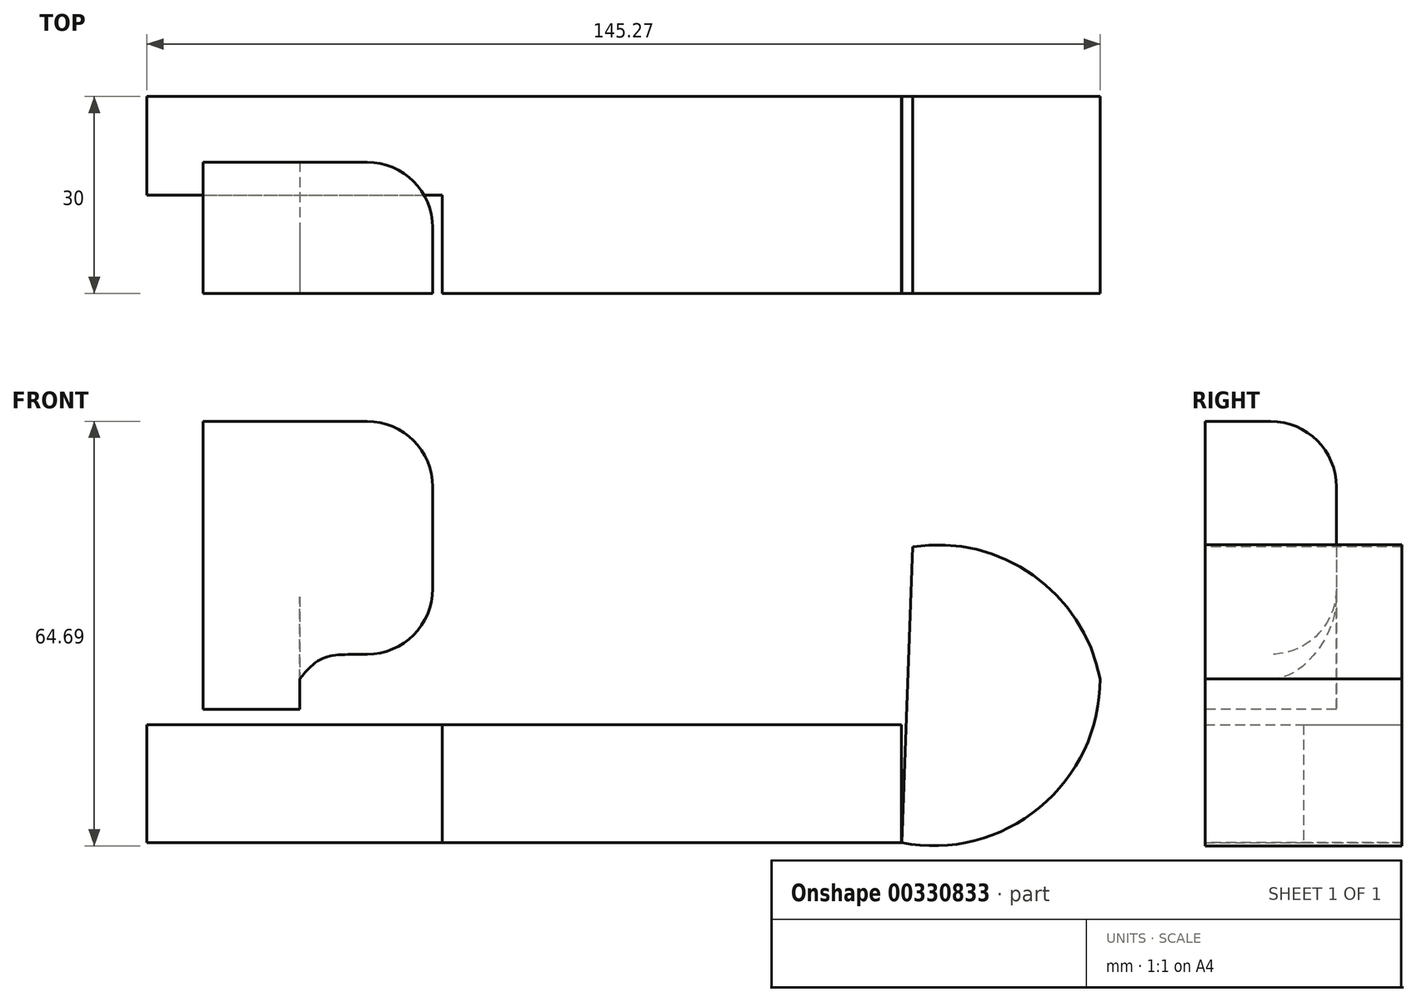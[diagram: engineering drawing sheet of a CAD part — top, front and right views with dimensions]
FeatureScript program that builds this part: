
annotation { "Feature Type Name" : "Feature", "Feature Type Description" : "" }
export const myFeature = defineFeature(function(context is Context, id is Id, definition is map)
    precondition{}
    {
        {
            var Q0;
            Q0=qCreatedBy(makeId("Top.planeOp"),FACE);
            var sketch = newSketch(context, id + "F0", { "sketchPlane" : qUnion([Q0])});
            skLineSegment(sketch, "E0.bottom", {"start": v(45.03, 0) * mm, "end": v(115, 0) * mm});
            skLineSegment(sketch, "E0.top", {"start": v(0, 30) * mm, "end": v(115, 30) * mm});
            skLineSegment(sketch, "E0.left", {"start": v(0, 15) * mm, "end": v(0, 30) * mm});
            skLineSegment(sketch, "E0.right", {"start": v(115, 0) * mm, "end": v(115, 30) * mm});
            skLineSegment(sketch, "E1", {"start": v(0, 30) * mm, "end": v(0, 15) * mm});
            skLineSegment(sketch, "E2", {"start": v(0, 15) * mm, "end": v(45.03, 15) * mm});
            skLineSegment(sketch, "E3", {"start": v(45.03, 0) * mm, "end": v(45.03, 15) * mm});
            skPoint(sketch, "E4.orphan", {"position": v(0, 0) * mm});
            skSolve(sketch);
        }
        {
            var Q0;
            Q0 = qSketchRegion(id + "F0", true);
            extrude(context, id + "F1", {"entities" : qUnion([Q0]), "depth" : 18 * mm});
        }
        {
            var Q0;
            Q0=qCreatedBy(makeId("Front.planeOp"),FACE);
            var sketch = newSketch(context, id + "F2", { "sketchPlane" : qUnion([Q0])});
            skLineSegment(sketch, "E5", {"start": v(115.04, 0) * mm, "end": v(124.63, 0) * mm});
            skArc(sketch, "E6", {"start": v(115.04, 0) * mm, "mid": v(136.04, 5.37) * mm, "end": v(145.27, 24.98) * mm});
            skArc(sketch, "E7", {"start": v(145.27, 24.98) * mm, "mid": v(135.05, 40.8) * mm, "end": v(116.72, 45.14) * mm});
            skLineSegment(sketch, "E8", {"start": v(116.72, 45.14) * mm, "end": v(115.04, 0) * mm});
            skSolve(sketch);
        }
        {
            var Q0;
            Q0 = qSketchRegion(id + "F2", true);
            extrude(context, id + "F3", {"entities" : qUnion([Q0]), "oppositeDirection" : true, "depth" : 30 * mm});
        }
        {
            var Q0;
            Q0=qCreatedBy(makeId("Front.planeOp"),FACE);
            var sketch = newSketch(context, id + "F4", { "sketchPlane" : qUnion([Q0])});
            skLineSegment(sketch, "E9", {"start": v(8.54, 64.23) * mm, "end": v(43.55, 64.23) * mm});
            skLineSegment(sketch, "E10", {"start": v(43.55, 64.23) * mm, "end": v(43.55, 34.02) * mm});
            skLineSegment(sketch, "E11", {"start": v(8.54, 64.23) * mm, "end": v(8.54, 20.34) * mm});
            skLineSegment(sketch, "E12", {"start": v(8.54, 20.34) * mm, "end": v(23.3, 20.34) * mm});
            skLineSegment(sketch, "E13", {"start": v(23.3, 20.34) * mm, "end": v(23.3, 24.96) * mm});
            skFitSpline(sketch, "E14", {"points": [v(23.3, 24.96) * mm, v(30.05, 28.69) * mm, v(41.42, 29.4) * mm, v(43.55, 34.02) * mm], "startDerivative": vector(22.6, 29.05) * mm, "endDerivative": vector(1.99, 31.8) * mm});
            skSolve(sketch);
        }
        {
            var Q0;
            Q0=makeQuery(id+"F4.imprint","IMPRINT",FACE,{"disambiguationData":[TD([[makeQuery(id+"F4.imprint","IMPRINT",EDGE,{"derivedFrom":sQuery(id+"F4.wireOp",EDGE,"E9")}),-1.0]])]});
            extrude(context, id + "F5", {"entities" : qUnion([Q0]), "oppositeDirection" : true, "depth" : 20 * mm});
        }
        {
            var Q0;
            Q0=makeQuery(id+"F5.opExtrude","CAP_EDGE",EDGE,{"disambiguationData":[OSD([sQuery(id+"F4.wireOp",EDGE,"E9")])],"isStart":false});
            fillet(context, id + "F6", {"entities" : qUnion([Q0]), "radius" : 10 * mm, "tangentPropagation" : true, "allowEdgeOverflow" : false});
        }
        {
            var Q0;
            Q0=makeQuery(id+"F5.opExtrude","CAP_EDGE",EDGE,{"disambiguationData":[OSD([sQuery(id+"F4.wireOp",EDGE,"E10")])],"isStart":false});
            fillet(context, id + "F7", {"entities" : qUnion([Q0]), "radius" : 10 * mm, "tangentPropagation" : true, "allowEdgeOverflow" : false});
        }
        {
            var Q0;
            Q0=makeQuery(id+"F7.opFillet","BLEND_EDGE",EDGE,{"blendedFrom":[makeQuery(id+"F5.opExtrude","CAP_EDGE",EDGE,{"disambiguationData":[OSD([sQuery(id+"F4.wireOp",EDGE,"E10")])],"isStart":false}),makeQuery(id+"F5.opExtrude","SWEPT_FACE",FACE,{"disambiguationData":[OSD([sQuery(id+"F4.wireOp",EDGE,"E14")])]})],"blendedInto":[makeQuery(id+"F5.opExtrude","SWEPT_FACE",FACE,{"disambiguationData":[OSD([sQuery(id+"F4.wireOp",EDGE,"E14")])]})]});
            var Q1;
            Q1=makeQuery(id+"F5.opExtrude","CAP_EDGE",EDGE,{"disambiguationData":[OSD([sQuery(id+"F4.wireOp",EDGE,"E14")])],"isStart":false});
            fillet(context, id + "F8", {"entities" : qUnion([Q0, Q1]), "radius" : 10 * mm, "tangentPropagation" : true, "allowEdgeOverflow" : false});
        }
    });
